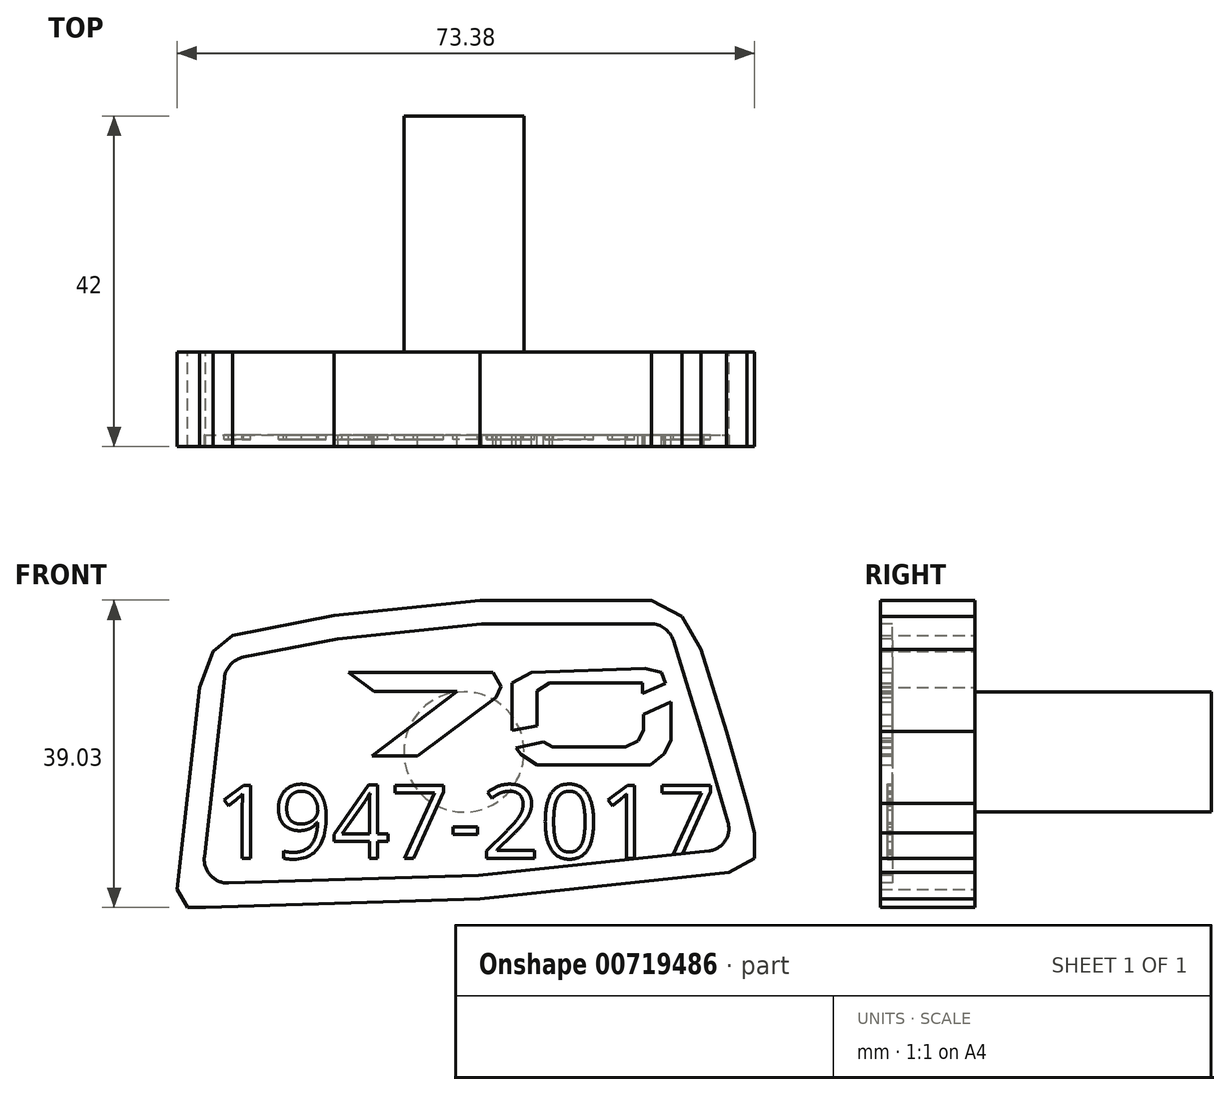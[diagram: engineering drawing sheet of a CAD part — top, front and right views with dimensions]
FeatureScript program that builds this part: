
annotation { "Feature Type Name" : "Feature", "Feature Type Description" : "" }
export const myFeature = defineFeature(function(context is Context, id is Id, definition is map)
    precondition{}
    {
        {
            var Q0;
            Q0=qCreatedBy(makeId("Front.planeOp"),FACE);
            var sketch = newSketch(context, id + "F0", { "sketchPlane" : qUnion([Q0])});
            skLineSegment(sketch, "E0", {"start": v(-12.84, -5.42) * mm, "end": v(-11.87, 3.14) * mm});
            skLineSegment(sketch, "E1", {"start": v(-11.87, 3.14) * mm, "end": v(-11.31, 4.66) * mm});
            skLineSegment(sketch, "E2", {"start": v(-11.31, 4.66) * mm, "end": v(-10.47, 5.34) * mm});
            skLineSegment(sketch, "E3", {"start": v(-10.47, 5.34) * mm, "end": v(-6.2, 6.18) * mm});
            skLineSegment(sketch, "E4", {"start": v(-6.2, 6.18) * mm, "end": v(0, 6.83) * mm});
            skLineSegment(sketch, "E5", {"start": v(0, 6.83) * mm, "end": v(4.82, 6.83) * mm});
            skLineSegment(sketch, "E6", {"start": v(4.82, 6.83) * mm, "end": v(7.26, 6.83) * mm});
            skLineSegment(sketch, "E7", {"start": v(7.26, 6.83) * mm, "end": v(8.54, 6.14) * mm});
            skLineSegment(sketch, "E8", {"start": v(8.54, 6.14) * mm, "end": v(9.34, 4.74) * mm});
            skLineSegment(sketch, "E9", {"start": v(9.34, 4.74) * mm, "end": v(10.42, 1.26) * mm});
            skLineSegment(sketch, "E10", {"start": v(10.42, 1.26) * mm, "end": v(11.3, -1.78) * mm});
            skLineSegment(sketch, "E11", {"start": v(11.3, -1.78) * mm, "end": v(11.62, -3.02) * mm});
            skLineSegment(sketch, "E12", {"start": v(11.62, -3.02) * mm, "end": v(11.62, -4.1) * mm});
            skLineSegment(sketch, "E13", {"start": v(11.62, -4.1) * mm, "end": v(10.54, -4.7) * mm});
            skLineSegment(sketch, "E14", {"start": v(10.54, -4.7) * mm, "end": v(0, -5.82) * mm});
            skLineSegment(sketch, "E15", {"start": v(0, -5.82) * mm, "end": v(-11.63, -6.18) * mm});
            skLineSegment(sketch, "E16", {"start": v(-11.63, -6.18) * mm, "end": v(-12.4, -6.18) * mm});
            skLineSegment(sketch, "E17", {"start": v(-12.4, -6.18) * mm, "end": v(-12.84, -5.42) * mm});
            skSolve(sketch);
        }
        {
            var Q0;
            Q0=makeQuery(id+"F0.imprint","IMPRINT",FACE,{"disambiguationData":[TD([[makeQuery(id+"F0.imprint","IMPRINT",EDGE,{"derivedFrom":sQuery(id+"F0.wireOp",EDGE,"E0")}),-1.0]])]});
            extrude(context, id + "F1", {"entities" : qUnion([Q0]), "depth" : 4 * mm, "offsetDistance" : 25 * mm});
        }
        {
            var Q0;
            Q0=makeQuery(id+"F1.opExtrude","CAP_FACE",FACE,{"disambiguationData":[OSD([sQuery(id+"F0.wireOp",EDGE,"E0"),sQuery(id+"F0.wireOp",EDGE,"E1"),sQuery(id+"F0.wireOp",EDGE,"E2"),sQuery(id+"F0.wireOp",EDGE,"E3"),sQuery(id+"F0.wireOp",EDGE,"E4"),sQuery(id+"F0.wireOp",EDGE,"E5"),sQuery(id+"F0.wireOp",EDGE,"E6"),sQuery(id+"F0.wireOp",EDGE,"E7"),sQuery(id+"F0.wireOp",EDGE,"E8"),sQuery(id+"F0.wireOp",EDGE,"E9"),sQuery(id+"F0.wireOp",EDGE,"E10"),sQuery(id+"F0.wireOp",EDGE,"E11"),sQuery(id+"F0.wireOp",EDGE,"E12"),sQuery(id+"F0.wireOp",EDGE,"E13"),sQuery(id+"F0.wireOp",EDGE,"E14"),sQuery(id+"F0.wireOp",EDGE,"E15"),sQuery(id+"F0.wireOp",EDGE,"E16"),sQuery(id+"F0.wireOp",EDGE,"E17")])],"isStart":false});
            var sketch = newSketch(context, id + "F2", { "sketchPlane" : qUnion([Q0])});
            skLineSegment(sketch, "E18.0", {"start": v(-0.07, -4.83) * mm, "end": v(-10.65, -5.15) * mm});
            skLineSegment(sketch, "E18.1", {"start": v(9.69, -3.79) * mm, "end": v(-0.07, -4.83) * mm});
            skLineSegment(sketch, "E18.2", {"start": v(-11.67, -4.04) * mm, "end": v(-10.82, 3.54) * mm});
            skLineSegment(sketch, "E18.3", {"start": v(9.46, 0.97) * mm, "end": v(10.5, -2.58) * mm});
            skLineSegment(sketch, "E18.4", {"start": v(-10.02, 4.41) * mm, "end": v(-6.04, 5.2) * mm});
            skLineSegment(sketch, "E18.5", {"start": v(-6.04, 5.2) * mm, "end": v(0.05, 5.83) * mm});
            skLineSegment(sketch, "E18.6", {"start": v(0.05, 5.83) * mm, "end": v(7.22, 5.83) * mm});
            skLineSegment(sketch, "E18.7", {"start": v(8.18, 5.12) * mm, "end": v(9.46, 0.97) * mm});
            skPoint(sketch, "E19.visualSharp", {"position": v(-10.74, 4.27) * mm});
            skArc(sketch, "E19.filletArc", {"start": v(-10.02, 4.41) * mm, "mid": v(-10.56, 4.1) * mm, "end": v(-10.82, 3.54) * mm});
            skPoint(sketch, "E20.visualSharp", {"position": v(-11.8, -5.19) * mm});
            skArc(sketch, "E20.filletArc", {"start": v(-11.67, -4.04) * mm, "mid": v(-11.42, -4.83) * mm, "end": v(-10.65, -5.15) * mm});
            skPoint(sketch, "E21.visualSharp", {"position": v(7.96, 5.83) * mm});
            skArc(sketch, "E21.filletArc", {"start": v(8.18, 5.12) * mm, "mid": v(7.81, 5.63) * mm, "end": v(7.22, 5.83) * mm});
            skPoint(sketch, "E22.visualSharp", {"position": v(10.8, -3.67) * mm});
            skArc(sketch, "E22.filletArc", {"start": v(9.69, -3.79) * mm, "mid": v(10.37, -3.38) * mm, "end": v(10.5, -2.58) * mm});
            skSolve(sketch);
        }
        {
            var Q0;
            Q0 = qSketchRegion(id + "F2", true);
            extrude(context, id + "F3", {"entities" : qUnion([Q0]), "operationType" : NewBodyOperationType.REMOVE, "oppositeDirection" : true, "depth" : 0.5 * mm, "offsetDistance" : 25 * mm});
        }
        {
            var Q0;
            Q0=makeQuery(id+"F3.boolean.opBoolean","COPY",FACE,{"derivedFrom":makeQuery(id+"F3.opExtrude","CAP_FACE",FACE,{"disambiguationData":[OSD([sQuery(id+"F2.wireOp",EDGE,"E18.0"),sQuery(id+"F2.wireOp",EDGE,"E18.1"),sQuery(id+"F2.wireOp",EDGE,"E18.2"),sQuery(id+"F2.wireOp",EDGE,"E18.3"),sQuery(id+"F2.wireOp",EDGE,"E18.4"),sQuery(id+"F2.wireOp",EDGE,"E18.5"),sQuery(id+"F2.wireOp",EDGE,"E18.6"),sQuery(id+"F2.wireOp",EDGE,"E18.7"),sQuery(id+"F2.wireOp",EDGE,"E19.filletArc"),sQuery(id+"F2.wireOp",EDGE,"E20.filletArc"),sQuery(id+"F2.wireOp",EDGE,"E21.filletArc"),sQuery(id+"F2.wireOp",EDGE,"E22.filletArc")])],"isStart":false})});
            var sketch = newSketch(context, id + "F4", { "sketchPlane" : qUnion([Q0])});
            skLineSegment(sketch, "E23", {"start": v(-5.57, 3.77) * mm, "end": v(-4.5, 2.95) * mm});
            skLineSegment(sketch, "E24", {"start": v(-4.5, 2.95) * mm, "end": v(-0.97, 2.95) * mm});
            skLineSegment(sketch, "E25", {"start": v(-0.97, 2.95) * mm, "end": v(-4.57, 0.23) * mm});
            skLineSegment(sketch, "E26", {"start": v(-4.57, 0.23) * mm, "end": v(-2.64, 0.23) * mm});
            skLineSegment(sketch, "E27", {"start": v(-2.64, 0.23) * mm, "end": v(0.66, 2.7) * mm});
            skLineSegment(sketch, "E28", {"start": v(0.66, 2.7) * mm, "end": v(0.88, 3.18) * mm});
            skLineSegment(sketch, "E29", {"start": v(0.88, 3.18) * mm, "end": v(0.55, 3.78) * mm});
            skLineSegment(sketch, "E30", {"start": v(-5.57, 3.77) * mm, "end": v(0.55, 3.78) * mm});
            skLineSegment(sketch, "E31", {"start": v(2.17, 3.77) * mm, "end": v(1.35, 3.32) * mm});
            skLineSegment(sketch, "E32", {"start": v(1.35, 3.32) * mm, "end": v(1.35, 2.3) * mm});
            skLineSegment(sketch, "E33", {"start": v(1.35, 2.3) * mm, "end": v(1.35, 1.3) * mm});
            skLineSegment(sketch, "E34", {"start": v(1.35, 1.3) * mm, "end": v(2.4, 1.5) * mm});
            skLineSegment(sketch, "E35", {"start": v(2.4, 1.5) * mm, "end": v(2.4, 3) * mm});
            skLineSegment(sketch, "E36", {"start": v(2.4, 3) * mm, "end": v(2.94, 3.32) * mm});
            skLineSegment(sketch, "E37", {"start": v(2.94, 3.32) * mm, "end": v(6.88, 3.32) * mm});
            skLineSegment(sketch, "E38", {"start": v(6.88, 2.87) * mm, "end": v(7.85, 3.3) * mm});
            skLineSegment(sketch, "E39", {"start": v(7.85, 3.3) * mm, "end": v(7.69, 3.77) * mm});
            skLineSegment(sketch, "E40", {"start": v(7.69, 3.77) * mm, "end": v(6.99, 3.94) * mm});
            skLineSegment(sketch, "E41", {"start": v(6.99, 3.94) * mm, "end": v(2.17, 3.77) * mm});
            skLineSegment(sketch, "E42", {"start": v(1.5, 0.58) * mm, "end": v(1.73, 0.3) * mm});
            skLineSegment(sketch, "E43", {"start": v(1.73, 0.3) * mm, "end": v(2.42, -0.14) * mm});
            skLineSegment(sketch, "E44", {"start": v(2.42, -0.14) * mm, "end": v(7.22, -0.14) * mm});
            skLineSegment(sketch, "E45", {"start": v(7.22, -0.14) * mm, "end": v(7.79, 0.31) * mm});
            skLineSegment(sketch, "E46", {"start": v(7.79, 0.31) * mm, "end": v(8.1, 0.88) * mm});
            skLineSegment(sketch, "E47", {"start": v(8.1, 0.88) * mm, "end": v(8.1, 2.52) * mm});
            skLineSegment(sketch, "E48", {"start": v(8.1, 2.52) * mm, "end": v(6.91, 2) * mm});
            skLineSegment(sketch, "E49", {"start": v(6.91, 2) * mm, "end": v(6.91, 1.32) * mm});
            skLineSegment(sketch, "E50", {"start": v(6.91, 1.32) * mm, "end": v(6.68, 0.87) * mm});
            skLineSegment(sketch, "E51", {"start": v(6.68, 0.87) * mm, "end": v(6.16, 0.62) * mm});
            skLineSegment(sketch, "E52", {"start": v(6.16, 0.62) * mm, "end": v(3.06, 0.62) * mm});
            skLineSegment(sketch, "E53", {"start": v(3.06, 0.62) * mm, "end": v(2.69, 0.83) * mm});
            skLineSegment(sketch, "E54", {"start": v(2.69, 0.83) * mm, "end": v(1.5, 0.58) * mm});
            skLineSegment(sketch, "E55", {"start": v(6.88, 3.32) * mm, "end": v(6.88, 2.87) * mm});
            skSolve(sketch);
        }
        {
            var Q0;
            Q0 = qSketchRegion(id + "F4", true);
            extrude(context, id + "F5", {"entities" : qUnion([Q0]), "operationType" : NewBodyOperationType.ADD, "depth" : 0.5 * mm, "offsetDistance" : 25 * mm});
        }
        {
            var Q0;
            Q0=makeQuery(id+"F3.boolean.opBoolean","COPY",FACE,{"derivedFrom":makeQuery(id+"F3.opExtrude","CAP_FACE",FACE,{"disambiguationData":[OSD([sQuery(id+"F2.wireOp",EDGE,"E18.0"),sQuery(id+"F2.wireOp",EDGE,"E18.1"),sQuery(id+"F2.wireOp",EDGE,"E18.2"),sQuery(id+"F2.wireOp",EDGE,"E18.3"),sQuery(id+"F2.wireOp",EDGE,"E18.4"),sQuery(id+"F2.wireOp",EDGE,"E18.5"),sQuery(id+"F2.wireOp",EDGE,"E18.6"),sQuery(id+"F2.wireOp",EDGE,"E18.7"),sQuery(id+"F2.wireOp",EDGE,"E19.filletArc"),sQuery(id+"F2.wireOp",EDGE,"E20.filletArc"),sQuery(id+"F2.wireOp",EDGE,"E21.filletArc"),sQuery(id+"F2.wireOp",EDGE,"E22.filletArc")])],"isStart":false})});
            var sketch = newSketch(context, id + "F6", { "sketchPlane" : qUnion([Q0])});
            skText(sketch, "E56", { "text": "1947-2017", "fontName": "OpenSans-Regular.ttf"});
            const initialGuessF6  = {"E56": [-0.01124, -0.0041, 1, 0, 0.00312]};
            skSetInitialGuess(sketch, initialGuessF6);
            skSolve(sketch);
        }
        {
            var Q0;
            Q0 = qSketchRegion(id + "F6", true);
            extrude(context, id + "F7", {"entities" : qUnion([Q0]), "operationType" : NewBodyOperationType.ADD, "depth" : 0.2 * mm, "offsetDistance" : 25 * mm});
        }
        {
            var Q0;
            Q0=makeQuery(id+"F1.opExtrude","CAP_FACE",FACE,{"disambiguationData":[OSD([sQuery(id+"F0.wireOp",EDGE,"E0"),sQuery(id+"F0.wireOp",EDGE,"E1"),sQuery(id+"F0.wireOp",EDGE,"E2"),sQuery(id+"F0.wireOp",EDGE,"E3"),sQuery(id+"F0.wireOp",EDGE,"E4"),sQuery(id+"F0.wireOp",EDGE,"E5"),sQuery(id+"F0.wireOp",EDGE,"E6"),sQuery(id+"F0.wireOp",EDGE,"E7"),sQuery(id+"F0.wireOp",EDGE,"E8"),sQuery(id+"F0.wireOp",EDGE,"E9"),sQuery(id+"F0.wireOp",EDGE,"E10"),sQuery(id+"F0.wireOp",EDGE,"E11"),sQuery(id+"F0.wireOp",EDGE,"E12"),sQuery(id+"F0.wireOp",EDGE,"E13"),sQuery(id+"F0.wireOp",EDGE,"E14"),sQuery(id+"F0.wireOp",EDGE,"E15"),sQuery(id+"F0.wireOp",EDGE,"E16"),sQuery(id+"F0.wireOp",EDGE,"E17")])],"isStart":true});
            var sketch = newSketch(context, id + "F8", { "sketchPlane" : qUnion([Q0])});
            skCircle(sketch, "E57", {"center": v(0.69, 0.4) * mm, "radius": 2.54 * mm});
            skSolve(sketch);
        }
        {
            var Q0;
            Q0=makeQuery(id+"F8.imprint","IMPRINT",FACE,{"disambiguationData":[TD([[makeQuery(id+"F8.imprint","IMPRINT",EDGE,{"derivedFrom":sQuery(id+"F8.wireOp",EDGE,"E57")}),1.0]])]});
            extrude(context, id + "F9", {"entities" : qUnion([Q0]), "operationType" : NewBodyOperationType.ADD, "depth" : 10 * mm, "offsetDistance" : 25 * mm});
        }
        {
            var Q0;
            Q0=makeQuery(id+"F1.opExtrude","SWEPT_BODY",BODY,{"disambiguationData":[OSD([sQuery(id+"F0.wireOp",EDGE,"E0"),sQuery(id+"F0.wireOp",EDGE,"E1"),sQuery(id+"F0.wireOp",EDGE,"E2"),sQuery(id+"F0.wireOp",EDGE,"E3"),sQuery(id+"F0.wireOp",EDGE,"E4"),sQuery(id+"F0.wireOp",EDGE,"E5"),sQuery(id+"F0.wireOp",EDGE,"E6"),sQuery(id+"F0.wireOp",EDGE,"E7"),sQuery(id+"F0.wireOp",EDGE,"E8"),sQuery(id+"F0.wireOp",EDGE,"E9"),sQuery(id+"F0.wireOp",EDGE,"E10"),sQuery(id+"F0.wireOp",EDGE,"E11"),sQuery(id+"F0.wireOp",EDGE,"E12"),sQuery(id+"F0.wireOp",EDGE,"E13"),sQuery(id+"F0.wireOp",EDGE,"E14"),sQuery(id+"F0.wireOp",EDGE,"E15"),sQuery(id+"F0.wireOp",EDGE,"E16"),sQuery(id+"F0.wireOp",EDGE,"E17")])]});
            var Q1;
            Q1=qCreatedBy(makeId("Origin.pointOp"),VERTEX);
            transform(context, id + "F10", {"entities" : qUnion([Q0]), "transformType" : TransformType.SCALE_UNIFORMLY, "scale" : 3, "scalePoint" : qUnion([Q1]), "makeCopy" : false});
        }
    });
